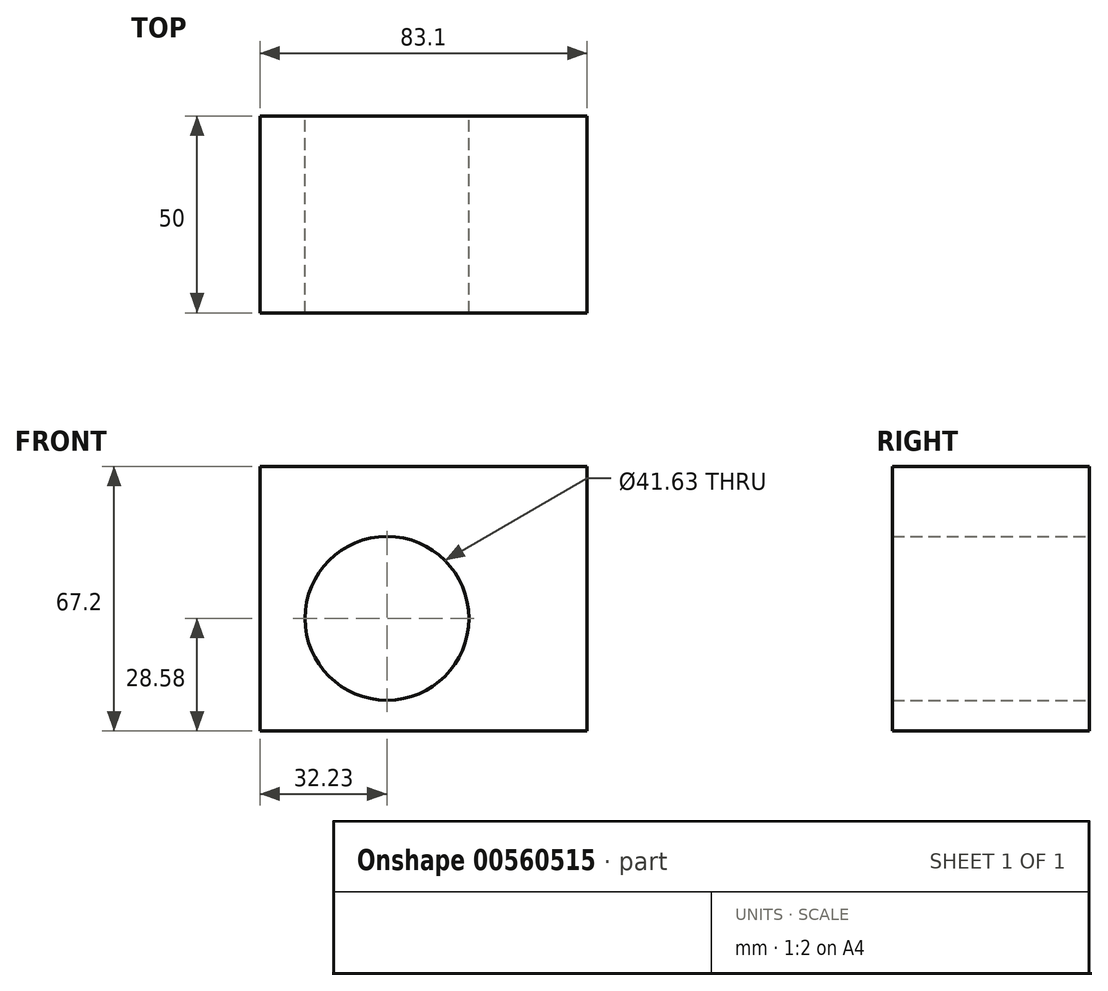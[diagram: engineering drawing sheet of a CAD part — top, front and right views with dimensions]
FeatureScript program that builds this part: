
annotation { "Feature Type Name" : "Feature", "Feature Type Description" : "" }
export const myFeature = defineFeature(function(context is Context, id is Id, definition is map)
    precondition{}
    {
        {
            var Q0;
            Q0=qCreatedBy(makeId("Front.planeOp"),FACE);
            var sketch = newSketch(context, id + "F0", { "sketchPlane" : qUnion([Q0])});
            skLineSegment(sketch, "E0.bottom", {"start": v(-37.67, 38.62) * mm, "end": v(45.43, 38.62) * mm});
            skLineSegment(sketch, "E0.top", {"start": v(-37.67, -28.58) * mm, "end": v(45.43, -28.58) * mm});
            skLineSegment(sketch, "E0.left", {"start": v(-37.67, 38.62) * mm, "end": v(-37.67, -28.58) * mm});
            skLineSegment(sketch, "E0.right", {"start": v(45.43, 38.62) * mm, "end": v(45.43, -28.58) * mm});
            skLineSegment(sketch, "E1", {"start": v(3.88, 38.62) * mm, "end": v(3.88, -28.58) * mm});
            skCircle(sketch, "E2", {"center": v(-5.44, 0) * mm, "radius": 20.82 * mm});
            skSolve(sketch);
        }
        {
            var Q0;
            Q0 = qSketchRegion(id + "F0", true);
            extrude(context, id + "F1", {"entities" : qUnion([Q0]), "depth" : 50 * mm, "offsetDistance" : 25 * mm});
        }
    });
